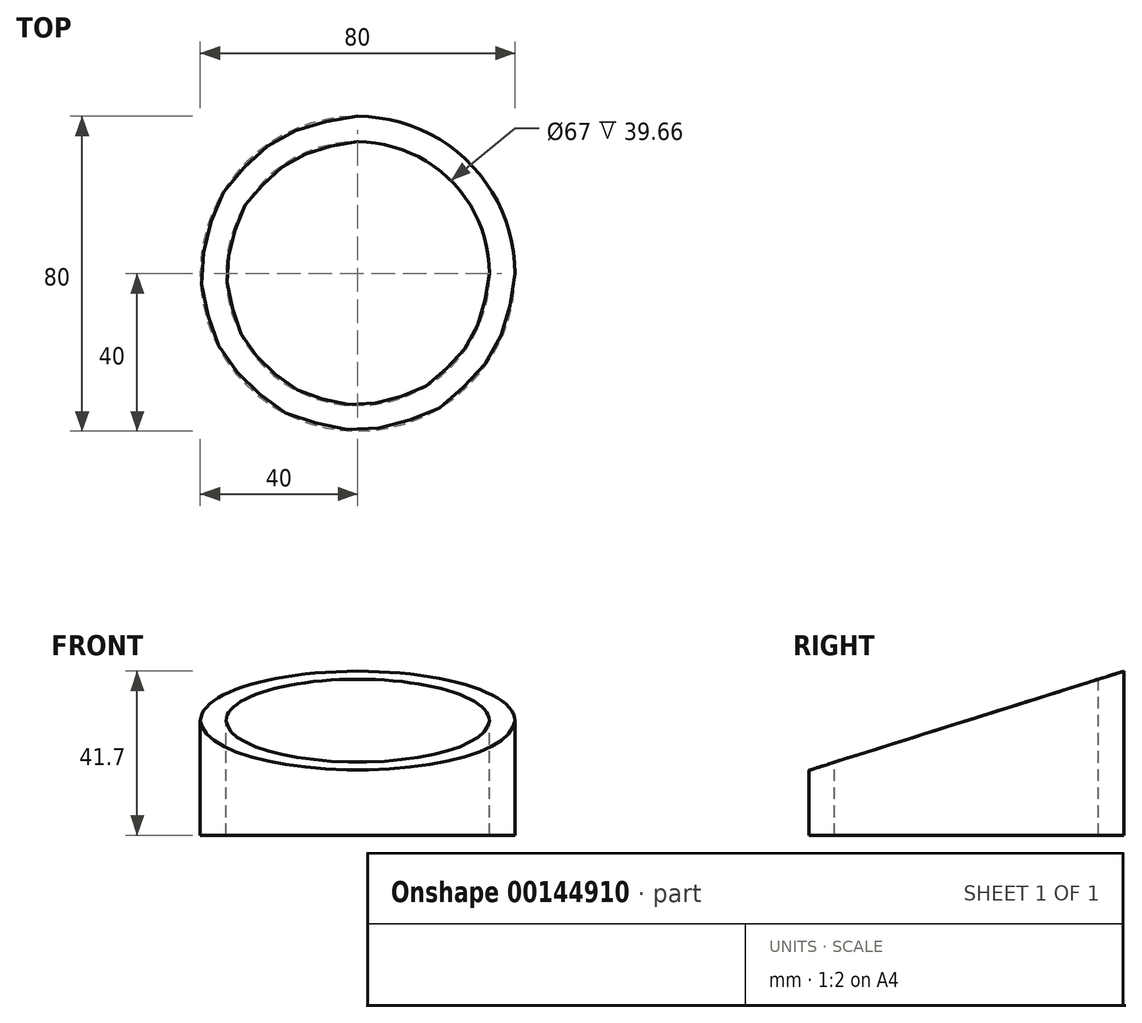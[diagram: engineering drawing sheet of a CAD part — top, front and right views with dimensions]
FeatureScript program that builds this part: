
annotation { "Feature Type Name" : "Feature", "Feature Type Description" : "" }
export const myFeature = defineFeature(function(context is Context, id is Id, definition is map)
    precondition{}
    {
        {
            var Q0;
            Q0=qCreatedBy(makeId("Top.planeOp"),FACE);
            var sketch = newSketch(context, id + "F0", { "sketchPlane" : qUnion([Q0])});
            skCircle(sketch, "E0", {"center": v(0, 0) * mm, "radius": 40 * mm});
            skCircle(sketch, "E1", {"center": v(0, 0) * mm, "radius": 33.5 * mm});
            skSolve(sketch);
        }
        {
            var Q0;
            Q0 = qSketchRegion(id + "F0", true);
            extrude(context, id + "F1", {"entities" : qUnion([Q0]), "endBound" : BoundingType.SYMMETRIC, "oppositeDirection" : true, "depth" : 41.7 * mm});
        }
        {
            var Q0;
            Q0=qCreatedBy(makeId("Right.planeOp"),FACE);
            var sketch = newSketch(context, id + "F2", { "sketchPlane" : qUnion([Q0])});
            skPoint(sketch, "E2.middle", {"position": v(0, 0) * mm});
            skLineSegment(sketch, "E3", {"start": v(40, 20.85) * mm, "end": v(-40, -4.33) * mm});
            skLineSegment(sketch, "E4", {"start": v(40, 20.85) * mm, "end": v(-40, 20.85) * mm});
            skLineSegment(sketch, "E5", {"start": v(-40, 20.85) * mm, "end": v(-40, -4.33) * mm});
            skSolve(sketch);
        }
        {
            var Q0;
            Q0 = qSketchRegion(id + "F2", true);
            extrude(context, id + "F3", {"entities" : qUnion([Q0]), "operationType" : NewBodyOperationType.REMOVE, "endBound" : BoundingType.SYMMETRIC, "depth" : 90 * mm});
        }
    });
